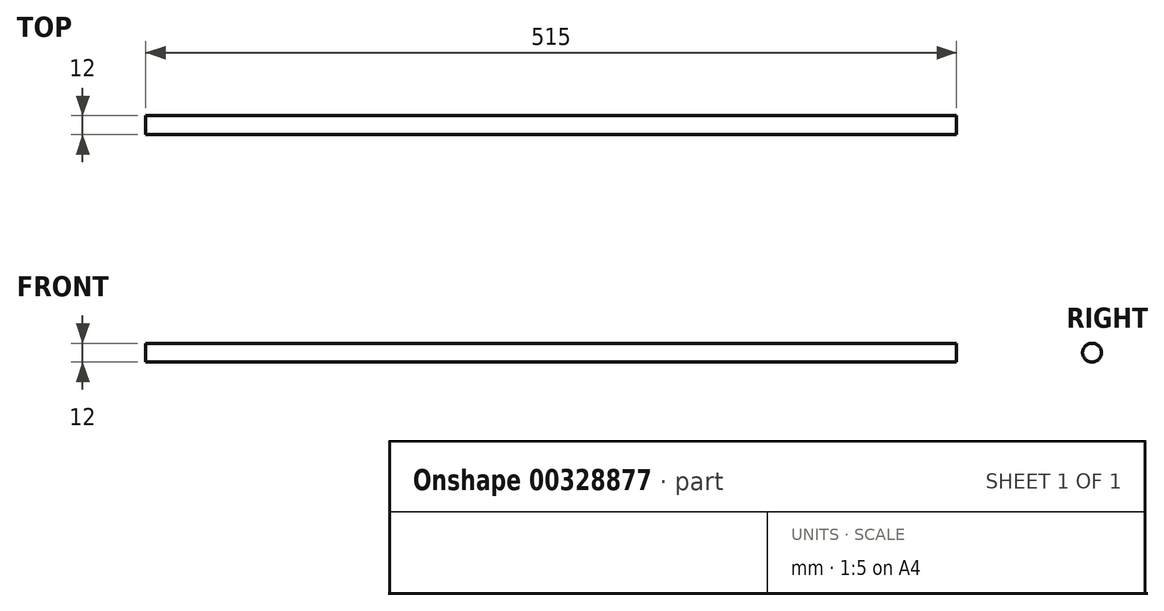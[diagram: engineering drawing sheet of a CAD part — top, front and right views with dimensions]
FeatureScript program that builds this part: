
annotation { "Feature Type Name" : "Feature", "Feature Type Description" : "" }
export const myFeature = defineFeature(function(context is Context, id is Id, definition is map)
    precondition{}
    {
        {
            var Q0;
            Q0=qCreatedBy(makeId("Right.planeOp"),FACE);
            var sketch = newSketch(context, id + "F0", { "sketchPlane" : qUnion([Q0])});
            skCircle(sketch, "E0", {"center": v(0, 0) * mm, "radius": 6 * mm});
            skSolve(sketch);
        }
        {
            var Q0;
            Q0=qSketchRegion(id+"F0",true);
            extrude(context, id + "F1", {"entities" : qUnion([Q0]), "endBound" : BoundingType.SYMMETRIC, "depth" : 515 * mm});
        }
    });
